# Revit family: Pilona Flexible HFLEX LED Solar
name_source: partatom
category: Furniture
units: mm (PartAtom-declared; Revit-internal decimal feet)

## family parameters
Always vertical = Yes
Cut with Voids When Loaded = No
OmniClass Number = 23.40.20.00
OmniClass Title = General Furniture and Specialties
Room Calculation Point = No
Shared = No
Work Plane-Based = No

## types (1)
- Pilona Flexible Luminosa Con LED Solar-HFLEXLEDSOL-1030mm
    A = 100 mm  [stored 0.328084 ft]
    Default Elevation = 0 mm  [stored 0 ft]
    Description = Pilona luminosa con LED solar, fabricada en poliuretano flexible en color negro (opcional en rojo, verde, amarillo o azul), resistente a los rayos
UV, con una banda reflectante.
    Fabricante = BENITO URBAN SL
    Ficha_Tecnica = https://www.benito.com
    H = 1030 mm  [stored 3.37927 ft]
    H1 = 190 mm  [stored 0.62336 ft]
    Material = Poliuretano flexible
    Material LED = LED verde
    Material reflectante = Aluminium
    Referencia = HFLEXLEDSOL
    Type Comments = Se fabrica en variante fija o móvil con bases de poliuretano o de acero inoxidable. También en versión con peana para instalación atornillada.
Supera una flexión de 1500 ciclos a 45º y 50 ciclos a 90º, sin daños. Clasificación “E” de comportamiento al fuego, según norma UNE-EN
13501-1:2007+A1:2010
    URL_Producto = https://www.benito.com

note: [stored X ft] marks values corroborated as IEEE doubles in the binary element streams (Revit-internal decimal feet)

## geometry (parser evidence)
native form markers: Blend x6, Sweep x2
no freeform markers — native parametric forms only
